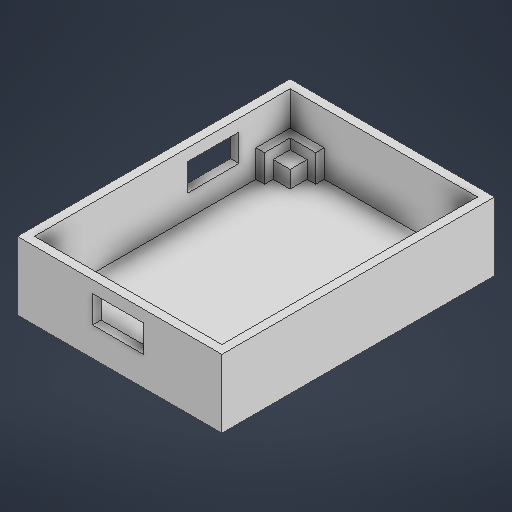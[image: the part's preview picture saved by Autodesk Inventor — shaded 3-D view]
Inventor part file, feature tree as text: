
AUTODESK INVENTOR PART (.ipt)
format: ipt  version: 2025 (Build 290162010, 162A)  size: 307,712 bytes
history: native  units: mm
features: extrude x9, sketch x4
ambient origin geometry x8: Origin, YZ Plane, XZ Plane, XY Plane, X Axis, Y Axis, Z Axis, Center Point
bodies: Solid1 (feature_tree)
feature tree (13):
  sketch  "Sketch1"  dims[d1=55.0mm d2=75.0mm]
  extrude  "Extrusion1"  Depth=75.0mm
  extrude  "Extrusion2"  Depth=60.0mm
  extrude  "Extrusion3"  Depth=2.0mm TaperAngle=0.0deg
  extrude  "Extrusion4"  Depth=20.0mm TaperAngle=0.0deg
  sketch  "Sketch3"  dims[d36=5.0mm d37=2.0mm d38=0.0mm]
  extrude  "Extrusion5"  Depth=1.5mm
  extrude  "Extrusion6"  Depth=10.0mm TaperAngle=0.0deg
  extrude  "Extrusion7"  Depth=8.0mm TaperAngle=0.0deg
  extrude  "Extrusion8"  Depth=8.0mm TaperAngle=0.0deg
  extrude  "Extrusion9"  Depth=8.0mm TaperAngle=0.0deg
  sketch  "Sketch2"  dims[d34=80.0mm d35=60.0mm]
  sketch  "Sketch4"  dims[d39=7.0mm d40=0.0mm d41=20.0mm d42=0.0mm d43=1.5mm d52=10.0mm d53=0.0mm d71=8.0mm d72=0.0mm d73=8.0mm d74=0.0mm d75=8.0mm d76=0.0mm d77=8.0mm d78=0.0mm d86=5.0mm d87=0.0mm d23=0.5mm d24=0.872665mm d25=0.5mm d26=0.872665mm]
